# Revit family: DesignMod-WD-100-1+Outlet
name_source: partatom
category: Electrical Equipment
revit_build: Autodesk Revit 2017 (Build: 20160225_1515(x64)
units: mm (PartAtom-declared; Revit-internal decimal feet)

## family parameters
Cut with Voids When Loaded = No
Host = Face
Panel Configuration = Two Columns, Circuits Across
Part Type = Panelboard
Room Calculation Point = No
Round Connector Dimension = Use Diameter
Shared = No

## types (1)
- DW-100-1
    Cover = cover
    Default Elevation = 4' - 0"
    Description = DesignMod Smoothline® Flush-mount wall plate system
    Display Receptacle Box = Yes
    Display Switch/Receptacle = Yes
    Display Wall Flange = Yes
    Manufacturer = DesignMod
    Manufacturer URL = www.DesignMod.com
    Model = DW-100-1
    Receptacle = Receptacle Box
    SmartBIM Object Version = 1
    Wall flange = wall flange
    display cover = Yes

## geometry (parser evidence)
native form markers: Sweep x6
no freeform markers — native parametric forms only
